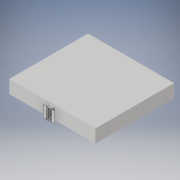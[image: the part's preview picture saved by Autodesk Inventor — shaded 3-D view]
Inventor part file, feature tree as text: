
AUTODESK INVENTOR PART (.ipt)
format: ipt  version: 2017 (Build 210142000, 142)  size: 580,608 bytes
history: native  units: in
note: dims shown in document units (in); Inventor stores cm internally (conversion verified against a paired STEP export)
features: extrude x9, sketch x7, delete_face x2
ambient origin geometry x8: Origin, YZ Plane, XZ Plane, XY Plane, X Axis, Y Axis, Z Axis, Center Point
bodies: Solid1 (feature_tree), Solid3 (feature_tree)
feature tree (18):
  extrude  "cubicals"  Depth=12.0in
  extrude  "floor"  Depth=2.5in
  extrude  "walls"  Depth=0.0833in
  extrude  "connection"  Depth=0.0833in
  extrude  "connection cut"  Depth=2.5in
  extrude  "ceiling"  Depth=0.0104in
  extrude  "door trim"  Depth=0.0104in
  extrude  "door trim top"  Depth=6.0in
  extrude  "floor trim"  Depth=6.0in
  delete_face  "Delete Face1"
  delete_face  "Delete Face2"
  sketch  "Sketch2"  dims[d2=4.5in d3=0.0in d4=12.0in]
  sketch  "Sketch3"  dims[d5=8.0in d7=2.5in]
  sketch  "Sketch6"  dims[d10=0.0833in d95=0.0833in]
  sketch  "Sketch7"  dims[d97=0.0833in d98=0.0833in]
  sketch  "Sketch8"  dims[d99=12.0in d100=8.0in d102=0.0833in d103=0.0833in d104=0.0833in d105=0.0833in]
  sketch  "Sketch9"  dims[d106=12.0in d107=8.0in d109=0.0833in d110=0.0833in d111=0.0833in d112=0.0833in d113=2.5in]
  sketch  "Sketch10"  dims[d114=2.5in d115=3.0in d117=3.0in d118=6.0in d120=6.0in d121=1.0in d122=0.0in d128=1.0in d129=1.0in d130=1.0in d131=1.0in d132=1.0in d133=1.0in d134=7.7746in d135=0.0in d160=1.0in d161=0.0in d171=1.0in d172=0.0in d173=1.0in d174=0.0in d191=1.4375in d192=6.6667in d193=2.875in d194=7.0in d195=6.6667in d200=0.0417in d201=0.1667in d202=1.0in d203=0.0in d204=0.1667in d205=1.0in d206=0.0in d207=0.0104in d208=0.3438in d209=0.0in d210=0.0104in d211=0.0104in d212=0.0104in]
